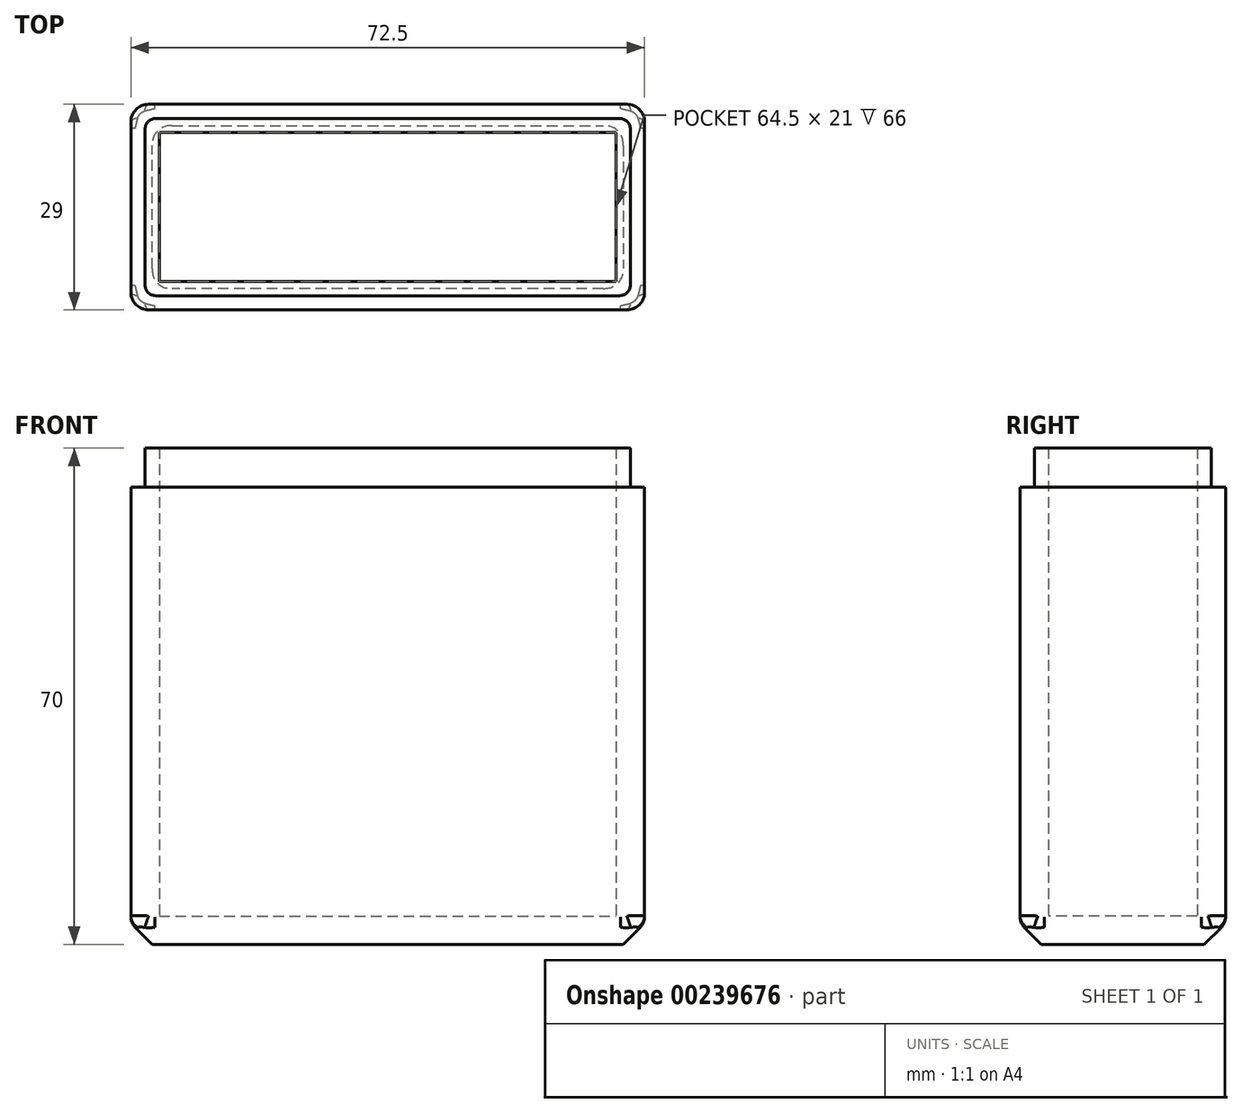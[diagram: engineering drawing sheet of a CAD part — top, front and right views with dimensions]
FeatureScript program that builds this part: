
annotation { "Feature Type Name" : "Feature", "Feature Type Description" : "" }
export const myFeature = defineFeature(function(context is Context, id is Id, definition is map)
    precondition{}
    {
        {
            var Q0;
            Q0=qCreatedBy(makeId("Top.planeOp"),FACE);
            var sketch = newSketch(context, id + "F0", { "sketchPlane" : qUnion([Q0])});
            skLineSegment(sketch, "E0.bottom", {"start": v(-23.07, 2.94) * mm, "end": v(41.43, 2.94) * mm});
            skLineSegment(sketch, "E0.top", {"start": v(-23.07, -18.06) * mm, "end": v(41.43, -18.06) * mm});
            skLineSegment(sketch, "E0.left", {"start": v(-23.07, 2.94) * mm, "end": v(-23.07, -18.06) * mm});
            skLineSegment(sketch, "E0.right", {"start": v(41.43, 2.94) * mm, "end": v(41.43, -18.06) * mm});
            skLineSegment(sketch, "E1.0", {"start": v(-27.07, 6.94) * mm, "end": v(45.43, 6.94) * mm});
            skLineSegment(sketch, "E1.1", {"start": v(-27.07, 6.94) * mm, "end": v(-27.07, -22.06) * mm});
            skLineSegment(sketch, "E1.2", {"start": v(-27.07, -22.06) * mm, "end": v(45.43, -22.06) * mm});
            skLineSegment(sketch, "E1.3", {"start": v(45.43, 6.94) * mm, "end": v(45.43, -22.06) * mm});
            skLineSegment(sketch, "E2.0", {"start": v(-25.07, 4.94) * mm, "end": v(43.43, 4.94) * mm});
            skLineSegment(sketch, "E2.1", {"start": v(-25.07, 4.94) * mm, "end": v(-25.07, -20.06) * mm});
            skLineSegment(sketch, "E2.2", {"start": v(-25.07, -20.06) * mm, "end": v(43.43, -20.06) * mm});
            skLineSegment(sketch, "E2.3", {"start": v(43.43, 4.94) * mm, "end": v(43.43, -20.06) * mm});
            skSolve(sketch);
        }
        {
            var Q0;
            Q0=makeQuery(id+"F0.imprint","IMPRINT",FACE,{"disambiguationData":[TD([[makeQuery(id+"F0.imprint","IMPRINT",EDGE,{"derivedFrom":sQuery(id+"F0.wireOp",EDGE,"E1.0")}),-1.0]])]});
            extrude(context, id + "F1", {"entities" : qUnion([Q0]), "depth" : 64.5 * mm});
        }
        {
            var Q0;
            Q0=makeQuery(id+"F0.imprint","IMPRINT",FACE,{"disambiguationData":[TD([[makeQuery(id+"F0.imprint","IMPRINT",EDGE,{"derivedFrom":sQuery(id+"F0.wireOp",EDGE,"E0.bottom")}),-1.0]])]});
            extrude(context, id + "F2", {"entities" : qUnion([Q0]), "operationType" : NewBodyOperationType.ADD, "depth" : 4 * mm});
        }
        {
            var Q0;
            Q0=makeQuery(id+"F0.imprint","IMPRINT",FACE,{"disambiguationData":[TD([[makeQuery(id+"F0.imprint","IMPRINT",EDGE,{"derivedFrom":sQuery(id+"F0.wireOp",EDGE,"E0.bottom")}),1.0]])]});
            extrude(context, id + "F3", {"entities" : qUnion([Q0]), "depth" : 70 * mm});
        }
        {
            var Q0;
            Q0=makeQuery(id+"F1.opExtrude","SWEPT_BODY",BODY,{"disambiguationData":[OSD([sQuery(id+"F0.wireOp",EDGE,"E1.0"),sQuery(id+"F0.wireOp",EDGE,"E1.1"),sQuery(id+"F0.wireOp",EDGE,"E1.2"),sQuery(id+"F0.wireOp",EDGE,"E1.3"),sQuery(id+"F0.wireOp",EDGE,"E2.0"),sQuery(id+"F0.wireOp",EDGE,"E2.1"),sQuery(id+"F0.wireOp",EDGE,"E2.2"),sQuery(id+"F0.wireOp",EDGE,"E2.3")])]});
            var Q1;
            Q1=makeQuery(id+"F2.opExtrude","SWEPT_BODY",BODY,{"disambiguationData":[OSD([sQuery(id+"F0.wireOp",EDGE,"E0.bottom"),sQuery(id+"F0.wireOp",EDGE,"E0.top"),sQuery(id+"F0.wireOp",EDGE,"E0.left"),sQuery(id+"F0.wireOp",EDGE,"E0.right")])]});
            var Q2;
            Q2=makeQuery(id+"F3.opExtrude","SWEPT_BODY",BODY,{"disambiguationData":[OSD([sQuery(id+"F0.wireOp",EDGE,"E0.bottom"),sQuery(id+"F0.wireOp",EDGE,"E0.top"),sQuery(id+"F0.wireOp",EDGE,"E0.left"),sQuery(id+"F0.wireOp",EDGE,"E0.right"),sQuery(id+"F0.wireOp",EDGE,"E2.0"),sQuery(id+"F0.wireOp",EDGE,"E2.1"),sQuery(id+"F0.wireOp",EDGE,"E2.2"),sQuery(id+"F0.wireOp",EDGE,"E2.3")])]});
            booleanBodies(context, id + "F4", {"operationType" : BooleanOperationType.UNION, "tools" : qUnion([Q0, Q1, Q2])});
        }
        {
            var Q0;
            {var subQ0=sQuery(id+"F0.wireOp",EDGE,"E2.3");var subQ1=sQuery(id+"F0.wireOp",EDGE,"E2.2");var subQ2=sQuery(id+"F0.wireOp",EDGE,"E2.1");var subQ3=sQuery(id+"F0.wireOp",EDGE,"E2.0");var subQ4=sQuery(id+"F0.wireOp",EDGE,"E0.right");var subQ5=sQuery(id+"F0.wireOp",EDGE,"E0.left");var subQ6=sQuery(id+"F0.wireOp",EDGE,"E0.top");var subQ7=sQuery(id+"F0.wireOp",EDGE,"E0.bottom");Q0=makeQuery(id+"F4.opBoolean","MERGE",FACE,{"derivedFrom":[makeQuery(id+"F1.opExtrude","CAP_FACE",FACE,{"disambiguationData":[OSD([sQuery(id+"F0.wireOp",EDGE,"E1.0"),sQuery(id+"F0.wireOp",EDGE,"E1.1"),sQuery(id+"F0.wireOp",EDGE,"E1.2"),sQuery(id+"F0.wireOp",EDGE,"E1.3"),subQ3,subQ2,subQ1,subQ0])],"isStart":true}),makeQuery(id+"F2.opExtrude","CAP_FACE",FACE,{"disambiguationData":[OSD([subQ7,subQ6,subQ5,subQ4])],"isStart":true}),makeQuery(id+"F3.opExtrude","CAP_FACE",FACE,{"disambiguationData":[OSD([subQ7,subQ6,subQ5,subQ4,subQ3,subQ2,subQ1,subQ0])],"isStart":true})]});}
            chamfer(context, id + "F5", {"entities" : qUnion([Q0]), "width" : 3 * mm, "tangentPropagation" : true});
        }
        {
            var Q0;
            Q0=makeQuery(id+"F5.opChamfer","BLEND_EDGE",EDGE,{"blendedFrom":[makeQuery(id+"F1.opExtrude","CAP_EDGE",EDGE,{"disambiguationData":[OSD([sQuery(id+"F0.wireOp",EDGE,"E1.0")])],"isStart":true}),makeQuery(id+"F1.opExtrude","CAP_EDGE",EDGE,{"disambiguationData":[OSD([sQuery(id+"F0.wireOp",EDGE,"E1.1")])],"isStart":true})],"blendedInto":[]});
            var Q1;
            Q1=makeQuery(id+"F5.opChamfer","BLEND_EDGE",EDGE,{"blendedFrom":[makeQuery(id+"F1.opExtrude","CAP_EDGE",EDGE,{"disambiguationData":[OSD([sQuery(id+"F0.wireOp",EDGE,"E1.1")])],"isStart":true}),makeQuery(id+"F1.opExtrude","CAP_EDGE",EDGE,{"disambiguationData":[OSD([sQuery(id+"F0.wireOp",EDGE,"E1.2")])],"isStart":true})],"blendedInto":[]});
            var Q2;
            Q2=makeQuery(id+"F5.opChamfer","BLEND_EDGE",EDGE,{"blendedFrom":[makeQuery(id+"F1.opExtrude","CAP_EDGE",EDGE,{"disambiguationData":[OSD([sQuery(id+"F0.wireOp",EDGE,"E1.2")])],"isStart":true}),makeQuery(id+"F1.opExtrude","CAP_EDGE",EDGE,{"disambiguationData":[OSD([sQuery(id+"F0.wireOp",EDGE,"E1.3")])],"isStart":true})],"blendedInto":[]});
            var Q3;
            Q3=makeQuery(id+"F5.opChamfer","BLEND_EDGE",EDGE,{"blendedFrom":[makeQuery(id+"F1.opExtrude","CAP_EDGE",EDGE,{"disambiguationData":[OSD([sQuery(id+"F0.wireOp",EDGE,"E1.0")])],"isStart":true}),makeQuery(id+"F1.opExtrude","CAP_EDGE",EDGE,{"disambiguationData":[OSD([sQuery(id+"F0.wireOp",EDGE,"E1.3")])],"isStart":true})],"blendedInto":[]});
            fillet(context, id + "F6", {"entities" : qUnion([Q0, Q1, Q2, Q3]), "radius" : 4 * mm, "tangentPropagation" : true, "allowEdgeOverflow" : false});
        }
        {
            var Q0;
            Q0=makeQuery(id+"F1.opExtrude","SWEPT_EDGE",EDGE,{"disambiguationData":[OSD([sQuery(id+"F0.wireOp",EDGE,"E1.2"),sQuery(id+"F0.wireOp",EDGE,"E1.3")])]});
            var Q1;
            Q1=makeQuery(id+"F1.opExtrude","SWEPT_EDGE",EDGE,{"disambiguationData":[OSD([sQuery(id+"F0.wireOp",EDGE,"E1.0"),sQuery(id+"F0.wireOp",EDGE,"E1.3")])]});
            var Q2;
            Q2=makeQuery(id+"F1.opExtrude","SWEPT_EDGE",EDGE,{"disambiguationData":[OSD([sQuery(id+"F0.wireOp",EDGE,"E1.0"),sQuery(id+"F0.wireOp",EDGE,"E1.1")])]});
            var Q3;
            Q3=makeQuery(id+"F1.opExtrude","SWEPT_EDGE",EDGE,{"disambiguationData":[OSD([sQuery(id+"F0.wireOp",EDGE,"E1.1"),sQuery(id+"F0.wireOp",EDGE,"E1.2")])]});
            fillet(context, id + "F7", {"entities" : qUnion([Q0, Q1, Q2, Q3]), "radius" : 2.5 * mm, "tangentPropagation" : true, "allowEdgeOverflow" : false});
        }
        {
            var Q0;
            Q0=makeQuery(id+"F3.opExtrude","SWEPT_EDGE",EDGE,{"disambiguationData":[OSD([sQuery(id+"F0.wireOp",EDGE,"E2.0"),sQuery(id+"F0.wireOp",EDGE,"E2.1")])]});
            var Q1;
            Q1=makeQuery(id+"F3.opExtrude","SWEPT_EDGE",EDGE,{"disambiguationData":[OSD([sQuery(id+"F0.wireOp",EDGE,"E2.1"),sQuery(id+"F0.wireOp",EDGE,"E2.2")])]});
            var Q2;
            Q2=makeQuery(id+"F3.opExtrude","SWEPT_EDGE",EDGE,{"disambiguationData":[OSD([sQuery(id+"F0.wireOp",EDGE,"E2.0"),sQuery(id+"F0.wireOp",EDGE,"E2.3")])]});
            var Q3;
            Q3=makeQuery(id+"F3.opExtrude","SWEPT_EDGE",EDGE,{"disambiguationData":[OSD([sQuery(id+"F0.wireOp",EDGE,"E2.2"),sQuery(id+"F0.wireOp",EDGE,"E2.3")])]});
            fillet(context, id + "F8", {"entities" : qUnion([Q0, Q1, Q2, Q3]), "radius" : 1.5 * mm, "tangentPropagation" : true, "allowEdgeOverflow" : false});
        }
        {
            var Q0;
            {var subQ0=sQuery(id+"F0.wireOp",EDGE,"E1.0");Q0=makeQuery(id+"F5.opChamfer","BLEND_EDGE",EDGE,{"blendedFrom":[makeQuery(id+"F1.opExtrude","CAP_EDGE",EDGE,{"disambiguationData":[OSD([subQ0])],"isStart":true}),makeQuery(id+"F1.opExtrude","SWEPT_FACE",FACE,{"disambiguationData":[OSD([subQ0])]})],"blendedInto":[makeQuery(id+"F1.opExtrude","SWEPT_FACE",FACE,{"disambiguationData":[OSD([subQ0])]})]});}
            fillet(context, id + "F9", {"entities" : qUnion([Q0]), "radius" : 2 * mm, "tangentPropagation" : true, "allowEdgeOverflow" : false});
        }
    });
